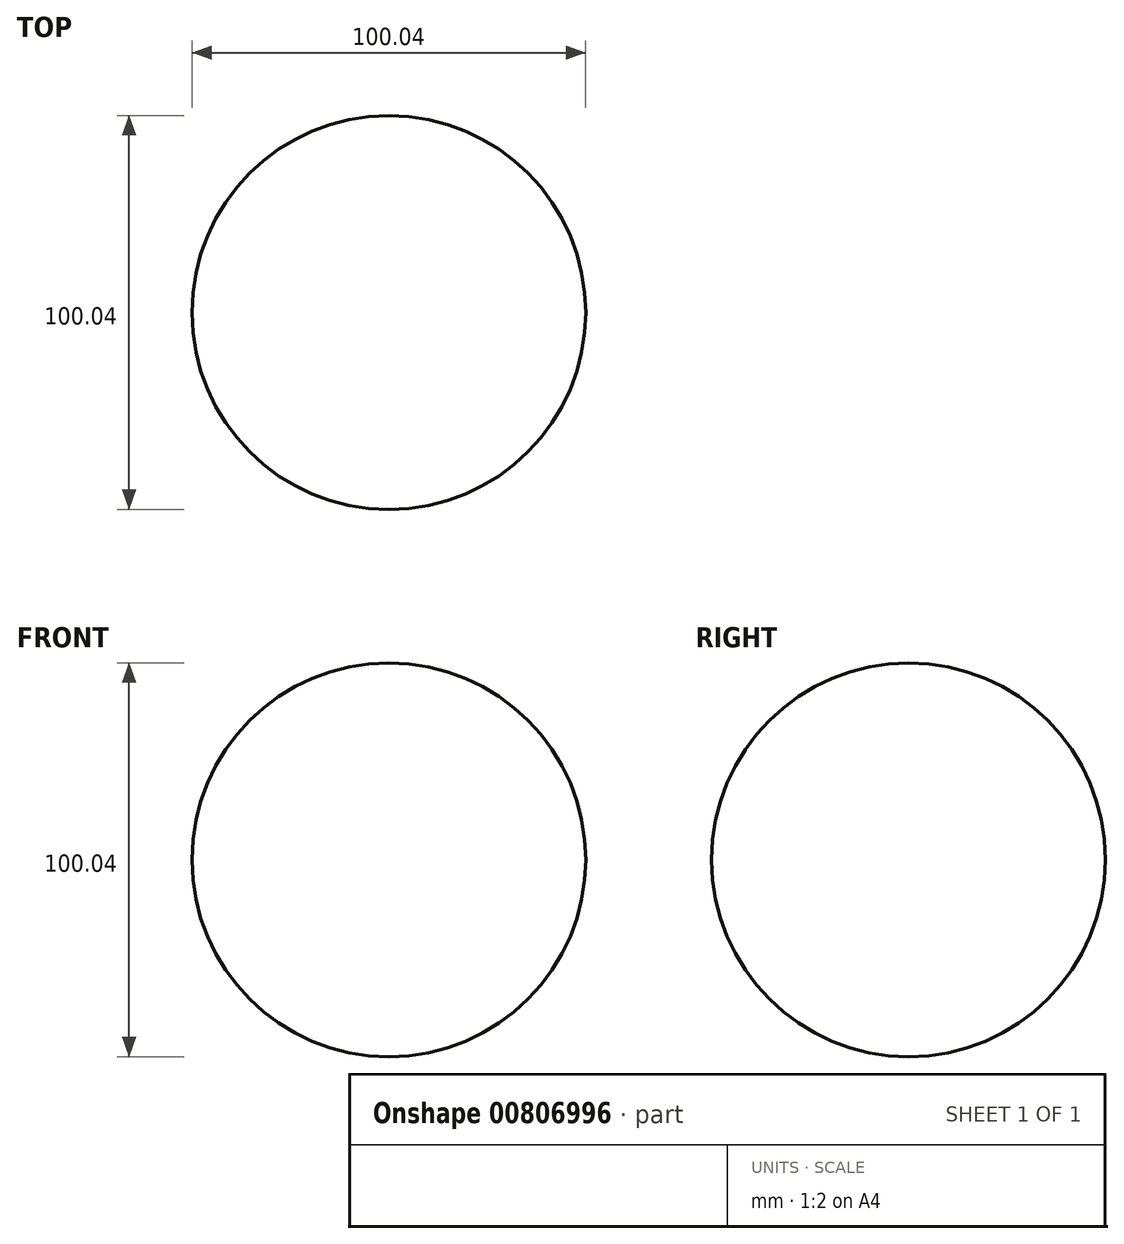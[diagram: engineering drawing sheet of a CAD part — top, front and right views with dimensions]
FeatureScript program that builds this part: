
annotation { "Feature Type Name" : "Feature", "Feature Type Description" : "" }
export const myFeature = defineFeature(function(context is Context, id is Id, definition is map)
    precondition{}
    {
        {
            var Q0;
            Q0=qCreatedBy(makeId("Front.planeOp"),FACE);
            var sketch = newSketch(context, id + "F0", { "sketchPlane" : qUnion([Q0])});
            skCircle(sketch, "E0", {"center": v(0, 0) * mm, "radius": 50.02 * mm});
            skLineSegment(sketch, "E1", {"start": v(0, 50.02) * mm, "end": v(0, -50.02) * mm});
            skSolve(sketch);
        }
        {
            var Q0;
            {var subQ0=sQuery(id+"F0.wireOp",EDGE,"E1");Q0=makeQuery(id+"F0.imprint","IMPRINT",FACE,{"disambiguationData":[TD([[makeQuery(id+"F0.imprint","IMPRINT",EDGE,{"derivedFrom":subQ0}),-1.0]])]});}
            var Q1;
            Q1=sQuery(id+"F0.wireOp",EDGE,"E1");
            revolve(context, id + "F1", {"surfaceOperationType" : NewSurfaceOperationType.NEW, "entities" : qUnion([Q0]), "axis" : qUnion([Q1]), "revolveType" : RevolveType.FULL});
        }
    });
